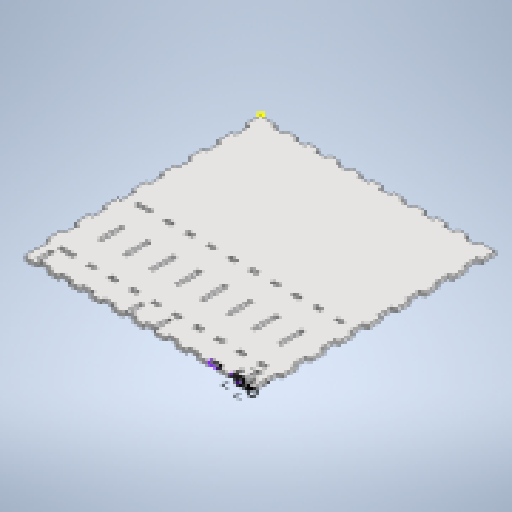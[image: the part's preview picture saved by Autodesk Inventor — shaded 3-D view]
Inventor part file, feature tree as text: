
AUTODESK INVENTOR PART (.ipt)
format: ipt  version: 2023 (Build 270158000, 158)  size: 599,040 bytes
history: native  units: mm
features: reference x208, other x23, sketch x8, extrude x6
ambient origin geometry x8: Origin, YZ Plane, XZ Plane, XY Plane, X Axis, Y Axis, Z Axis, Center Point
bodies: Solid1 (feature_tree)
feature tree (245):
  extrude  "Extrusion1"  Depth=330.0mm
  extrude  "Extrusion2"  Depth=10.0mm TaperAngle=0.0deg
  extrude  "Extrusion3"  Depth=6.0mm
  extrude  "Extrusion4"  Depth=5.0mm TaperAngle=0.0deg
  extrude  "Extrusion5"  Depth=5.0mm TaperAngle=0.0deg
  extrude  "Extrusion6"  Depth=6.0mm
  sketch  "Sketch9"  dims[d17=6.0mm]
  sketch  "Sketch10"  dims[d18=1.0mm d19=5.0mm d20=0.0mm d21=6.0mm d22=6.0mm]
  sketch  "Sketch1"  dims[d0=330.0mm d1=330.0mm]
  sketch  "Sketch4"  dims[d2=5.0mm d3=0.0mm d4=10.0mm d5=0.0mm]
  reference  "Reference6"
  reference  "Reference7"
  reference  "Reference8"
  reference  "Reference9"
  reference  "Reference10"
  reference  "Reference11"
  reference  "Reference12"
  reference  "Reference13"
  reference  "Reference14"
  reference  "Reference15"
  reference  "Reference16"
  reference  "Reference17"
  reference  "Reference18"
  reference  "Reference19"
  reference  "Reference20"
  reference  "Reference21"
  reference  "Reference22"
  reference  "Reference23"
  reference  "Reference24"
  reference  "Reference25"
  reference  "Reference26"
  reference  "Reference27"
  reference  "Reference28"
  reference  "Reference29"
  reference  "Reference30"
  reference  "Reference31"
  reference  "Reference32"
  reference  "Reference33"
  reference  "Reference34"
  reference  "Reference35"
  reference  "Reference36"
  reference  "Reference37"
  reference  "Reference38"
  reference  "Reference39"
  reference  "Reference40"
  reference  "Reference41"
  reference  "Reference42"
  reference  "Reference43"
  reference  "Reference44"
  reference  "Reference45"
  reference  "Reference46"
  reference  "Reference47"
  reference  "Reference48"
  reference  "Reference49"
  reference  "Reference50"
  reference  "Reference51"
  reference  "Reference52"
  reference  "Reference53"
  reference  "Reference54"
  reference  "Reference55"
  reference  "Reference56"
  reference  "Reference57"
  reference  "Reference58"
  reference  "Reference59"
  reference  "Reference60"
  reference  "Reference61"
  reference  "Reference62"
  reference  "Reference63"
  reference  "Reference64"
  reference  "Reference65"
  reference  "Reference66"
  reference  "Reference67"
  reference  "Reference68"
  reference  "Reference69"
  reference  "Reference70"
  reference  "Reference71"
  reference  "Reference72"
  reference  "Reference73"
  reference  "Reference74"
  reference  "Reference75"
  reference  "Reference76"
  reference  "Reference77"
  reference  "Reference78"
  reference  "Reference79"
  reference  "Reference80"
  reference  "Reference81"
  reference  "Reference82"
  reference  "Reference83"
  reference  "Reference84"
  reference  "Reference85"
  reference  "Reference86"
  reference  "Reference87"
  reference  "Reference88"
  reference  "Reference89"
  reference  "Reference90"
  reference  "Reference91"
  reference  "Reference92"
  reference  "Reference93"
  reference  "Reference94"
  reference  "Reference95"
  reference  "Reference96"
  reference  "Reference97"
  reference  "Reference98"
  reference  "Reference99"
  reference  "Reference100"
  reference  "Reference101"
  reference  "Reference102"
  reference  "Reference103"
  reference  "Reference104"
  reference  "Reference105"
  reference  "Reference106"
  reference  "Reference107"
  reference  "Reference109"
  reference  "Reference110"
  reference  "Reference111"
  reference  "Reference112"
  reference  "Reference113"
  reference  "Reference114"
  reference  "Reference115"
  reference  "Reference116"
  reference  "Reference117"
  reference  "Reference118"
  reference  "Reference119"
  reference  "Reference120"
  reference  "Reference121"
  reference  "Reference122"
  reference  "Reference123"
  reference  "Reference124"
  reference  "Reference125"
  reference  "Reference126"
  reference  "Reference127"
  reference  "Reference128"
  reference  "Reference129"
  reference  "Reference130"
  reference  "Reference131"
  reference  "Reference132"
  reference  "Reference133"
  reference  "Reference134"
  reference  "Reference135"
  reference  "Reference136"
  reference  "Reference137"
  reference  "Reference138"
  reference  "Reference139"
  reference  "Reference140"
  reference  "Reference141"
  reference  "Reference142"
  reference  "Reference143"
  reference  "Reference144"
  reference  "Reference145"
  reference  "Reference146"
  reference  "Reference147"
  reference  "Reference148"
  reference  "Reference149"
  reference  "Reference150"
  reference  "Reference151"
  reference  "Reference152"
  reference  "Reference155"
  reference  "Reference159"
  reference  "Reference160"
  reference  "Reference161"
  reference  "Reference163"
  reference  "Reference164"
  reference  "Reference165"
  reference  "Reference166"
  reference  "Reference167"
  reference  "Reference168"
  reference  "Reference169"
  reference  "Reference170"
  reference  "Reference171"
  reference  "Reference172"
  reference  "Reference173"
  reference  "Reference174"
  reference  "Reference175"
  reference  "Reference176"
  reference  "Reference177"
  reference  "Reference178"
  reference  "Reference179"
  reference  "Reference180"
  reference  "Reference181"
  reference  "Reference182"
  reference  "Reference183"
  reference  "Reference184"
  reference  "Reference185"
  reference  "Reference186"
  reference  "Reference187"
  reference  "Reference188"
  reference  "Reference189"
  reference  "Reference190"
  reference  "Reference191"
  sketch  "Sketch5"  dims[d6=10.0mm d7=0.0mm d8=6.0mm]
  reference  "Reference199"
  reference  "Reference200"
  reference  "Reference201"
  reference  "Reference202"
  reference  "Reference203"
  reference  "Reference204"
  reference  "Reference205"
  reference  "Reference206"
  reference  "Reference207"
  reference  "Reference208"
  reference  "Reference209"
  reference  "Reference210"
  reference  "Reference211"
  reference  "Reference212"
  reference  "Reference213"
  reference  "Reference214"
  reference  "Reference215"
  reference  "Reference216"
  reference  "Reference217"
  reference  "Reference218"
  reference  "Reference219"
  reference  "Reference220"
  reference  "Reference221"
  reference  "Reference222"
  reference  "Reference223"
  reference  "Reference224"
  reference  "Reference225"
  reference  "Reference226"
  reference  "Reference227"
  sketch  "Sketch6"  dims[d9=6.0mm d10=5.0mm d11=0.0mm]
  sketch  "Sketch7"  dims[d12=6.0mm d13=5.0mm d14=0.0mm]
  sketch  "Sketch8"  dims[d15=6.0mm d16=6.0mm]
  other  "<userpath>\OneDrive\ClawdDrive\Objet3D\Clawd4\Assembly1.iam"
  other  "Assembly1.iam"
  other  "BackFrontPannelFAN:1"
  other  "Side:1"
  other  "Side:2"
  other  "BackFrontPannel:1"
  other  "motherBoardHolder:1"
  other  "HddSpacerPlate:7"
  other  "HddSpacerPlate:8"
  other  "HddSpacerPlate:5"
  other  "HddSpacerPlate:4"
  other  "HddSpacerPlate:6"
  other  "HddSpacerPlate:3"
  other  "HddSpacerPlate:1"
  other  "HddSpacerPlate:2"
  other  "HddBigSeparator:2"
  other  "HddFanPlate:1"
  other  "FanVerticalPlate:1"
  other  "FanVerticalPlate:2"
  other  "FanVerticalPlate:3"
  other  "FanVerticalPlate:4"
  other  "FANsuport:2"
  other  "FANsuport:1"
